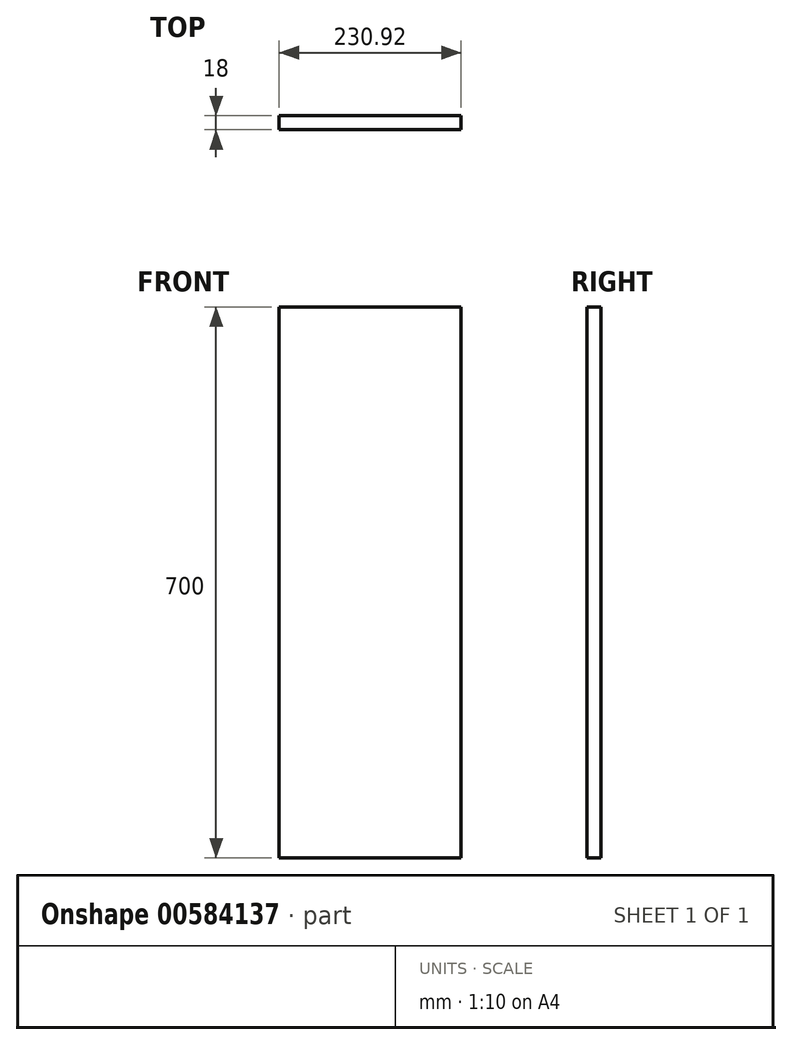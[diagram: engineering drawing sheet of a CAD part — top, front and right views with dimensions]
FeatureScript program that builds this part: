
annotation { "Feature Type Name" : "Feature", "Feature Type Description" : "" }
export const myFeature = defineFeature(function(context is Context, id is Id, definition is map)
    precondition{}
    {
        {
            var Q0;
            Q0=qCreatedBy(makeId("Front.planeOp"),FACE);
            var sketch = newSketch(context, id + "F0", { "sketchPlane" : qUnion([Q0])});
            skLineSegment(sketch, "E0", {"start": v(0, 0) * mm, "end": v(0, -700) * mm});
            skLineSegment(sketch, "E1", {"start": v(0, -700) * mm, "end": v(230.92, -700) * mm});
            skLineSegment(sketch, "E2", {"start": v(230.92, -700) * mm, "end": v(230.92, 0) * mm});
            skLineSegment(sketch, "E3", {"start": v(230.92, 0) * mm, "end": v(0, 0) * mm});
            skSolve(sketch);
        }
        {
            var Q0;
            Q0 = qSketchRegion(id + "F0", true);
            extrude(context, id + "F1", {"entities" : qUnion([Q0]), "depth" : 18 * mm, "offsetDistance" : 25 * mm});
        }
    });
